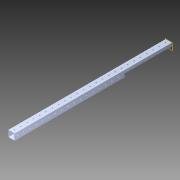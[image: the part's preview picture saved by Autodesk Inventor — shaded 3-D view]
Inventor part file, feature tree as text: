
AUTODESK INVENTOR PART (.ipt)
format: ipt  version: 2014 (Build 180170000, 170)  size: 1,343,488 bytes
history: native  units: in
note: dims shown in document units (in); Inventor stores cm internally (conversion verified against a paired STEP export)
features: extrude x3, sketch x3, reference x2, pattern_circular x1, other x1, plane x1, imported_body x1
ambient origin geometry x8: Origin, YZ Plane, XZ Plane, XY Plane, X Axis, Y Axis, Z Axis, Center Point
bodies: Body1 (feature_tree)
feature tree (12):
  pattern_circular  "CirPattern2"
  other  "217-3426-STEP1"
  plane  "Work Plane1"
  extrude  "Extrusion1"  Depth=3937.0079in TaperAngle=0.0deg
  extrude  "Extrusion3"  Depth=0.5in
  extrude  "Extrusion4"  Depth=0.0787in
  imported_body  "Base1"
  sketch  "Sketch1"  dims[d0=-25.0in d1=3937.0079in d2=0.0in]
  sketch  "Sketch4"  dims[d10=3.937in d11=0.0in d12=0.5in]
  reference  "Reference2"
  reference  "Reference3"
  sketch  "Sketch5"  dims[d13=7.5in d14=0.0787in d15=3.937in d16=0.0in]
